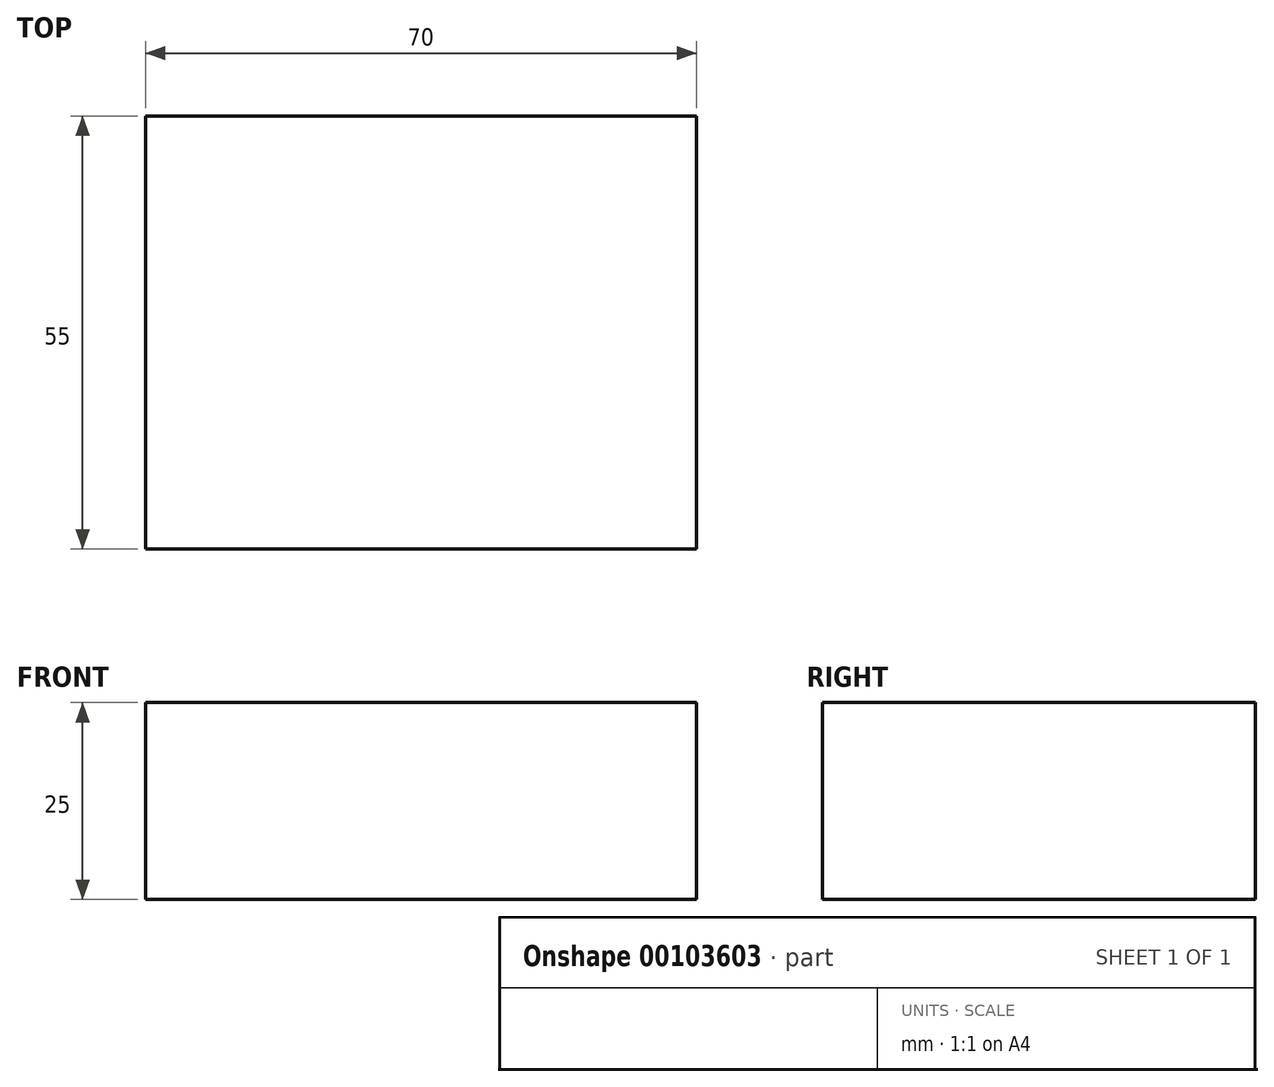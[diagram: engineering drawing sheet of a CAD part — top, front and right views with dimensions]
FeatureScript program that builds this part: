
annotation { "Feature Type Name" : "Feature", "Feature Type Description" : "" }
export const myFeature = defineFeature(function(context is Context, id is Id, definition is map)
    precondition{}
    {
        {
            var Q0;
            Q0=qCreatedBy(makeId("Front.planeOp"),FACE);
            var sketch = newSketch(context, id + "F0", { "sketchPlane" : qUnion([Q0])});
            skLineSegment(sketch, "E0.bottom", {"start": v(-27.5, 40.61) * mm, "end": v(42.5, 40.61) * mm});
            skLineSegment(sketch, "E0.top", {"start": v(-27.5, 15.61) * mm, "end": v(42.5, 15.61) * mm});
            skLineSegment(sketch, "E0.left", {"start": v(-27.5, 40.61) * mm, "end": v(-27.5, 15.61) * mm});
            skLineSegment(sketch, "E0.right", {"start": v(42.5, 40.61) * mm, "end": v(42.5, 15.61) * mm});
            skSolve(sketch);
        }
        {
            var Q0;
            Q0 = qSketchRegion(id + "F0", true);
            extrude(context, id + "F1", {"entities" : qUnion([Q0]), "depth" : 55 * mm});
        }
    });
